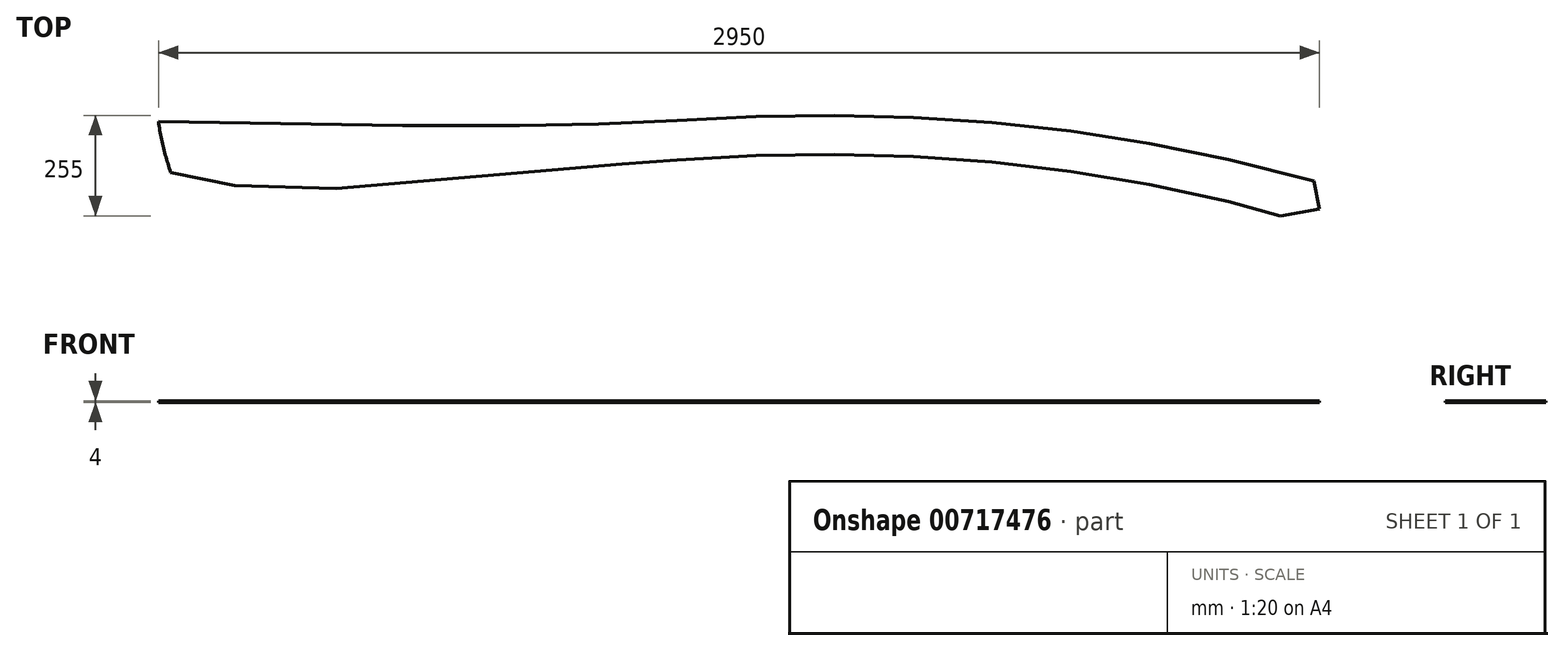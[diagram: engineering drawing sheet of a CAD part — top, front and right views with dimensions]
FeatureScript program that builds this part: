
annotation { "Feature Type Name" : "Feature", "Feature Type Description" : "" }
export const myFeature = defineFeature(function(context is Context, id is Id, definition is map)
    precondition{}
    {
        {
            var Q0;
            Q0=qCreatedBy(makeId("Top.planeOp"),FACE);
            var sketch = newSketch(context, id + "F0", { "sketchPlane" : qUnion([Q0])});
            skLineSegment(sketch, "E0", {"start": v(533, 272) * mm, "end": v(431, 192) * mm});
            skLineSegment(sketch, "E1", {"start": v(113, 312) * mm, "end": v(275, 279) * mm});
            skLineSegment(sketch, "E2", {"start": v(2933, 202) * mm, "end": v(3032, 219) * mm});
            skLineSegment(sketch, "E3", {"start": v(3017, 290) * mm, "end": v(3032, 219) * mm});
            skLineSegment(sketch, "E4", {"start": v(82, 442) * mm, "end": v(702, 431) * mm});
            skLineSegment(sketch, "E5", {"start": v(533, 272) * mm, "end": v(1260, 334) * mm});
            skLineSegment(sketch, "E6", {"start": v(275, 279) * mm, "end": v(533, 272) * mm});
            skArc(sketch, "E7", {"start": v(0, 0) * mm, "mid": v(29.12, 165.92) * mm, "end": v(113, 312) * mm});
            skArc(sketch, "E8", {"start": v(301, 0) * mm, "mid": v(294.49, 140.1) * mm, "end": v(275, 279) * mm});
            skLineSegment(sketch, "E9", {"start": v(301, 0) * mm, "end": v(0, 0) * mm});
            skArc(sketch, "E10", {"start": v(414, 0) * mm, "mid": v(418.26, 96.38) * mm, "end": v(431, 192) * mm});
            skLineSegment(sketch, "E11", {"start": v(301, 0) * mm, "end": v(414, 0) * mm});
            skPoint(sketch, "E12.orphan", {"position": v(2800, 0) * mm});
            skPoint(sketch, "E13.orphan", {"position": v(2600, 0) * mm});
            skPoint(sketch, "E14.orphan", {"position": v(2400, 0) * mm});
            skPoint(sketch, "E15.orphan", {"position": v(2200, 0) * mm});
            skPoint(sketch, "E16.orphan", {"position": v(2000, 0) * mm});
            skPoint(sketch, "E17.orphan", {"position": v(1400, 0) * mm});
            skPoint(sketch, "E18.orphan", {"position": v(1600, 0) * mm});
            skPoint(sketch, "E19.orphan", {"position": v(1800, 0) * mm});
            skLineSegment(sketch, "E20", {"start": v(1260, 334) * mm, "end": v(1400, 344) * mm});
            skLineSegment(sketch, "E21", {"start": v(1400, 344) * mm, "end": v(1600, 355) * mm});
            skLineSegment(sketch, "E22", {"start": v(1600, 355) * mm, "end": v(1800, 358) * mm});
            skLineSegment(sketch, "E23", {"start": v(1800, 358) * mm, "end": v(2000, 353) * mm});
            skLineSegment(sketch, "E24", {"start": v(2000, 353) * mm, "end": v(2200, 339) * mm});
            skLineSegment(sketch, "E25", {"start": v(2200, 339) * mm, "end": v(2400, 315) * mm});
            skLineSegment(sketch, "E26", {"start": v(2400, 315) * mm, "end": v(2600, 282) * mm});
            skLineSegment(sketch, "E27", {"start": v(2600, 282) * mm, "end": v(2800, 238) * mm});
            skLineSegment(sketch, "E28", {"start": v(2800, 238) * mm, "end": v(2933, 202) * mm});
            skLineSegment(sketch, "E29", {"start": v(3017, 290) * mm, "end": v(2800, 345) * mm});
            skLineSegment(sketch, "E30", {"start": v(2800, 345) * mm, "end": v(2600, 386) * mm});
            skLineSegment(sketch, "E31", {"start": v(2600, 386) * mm, "end": v(2400, 417) * mm});
            skLineSegment(sketch, "E32", {"start": v(2400, 417) * mm, "end": v(2200, 439) * mm});
            skLineSegment(sketch, "E33", {"start": v(2200, 439) * mm, "end": v(2000, 452) * mm});
            skLineSegment(sketch, "E34", {"start": v(2000, 452) * mm, "end": v(1800, 457) * mm});
            skLineSegment(sketch, "E35", {"start": v(1800, 457) * mm, "end": v(1600, 454) * mm});
            skLineSegment(sketch, "E36", {"start": v(1600, 454) * mm, "end": v(1400, 444) * mm});
            skLineSegment(sketch, "E37", {"start": v(702, 431) * mm, "end": v(1000, 431) * mm});
            skLineSegment(sketch, "E38", {"start": v(1000, 431) * mm, "end": v(1200, 435) * mm});
            skLineSegment(sketch, "E39", {"start": v(1200, 435) * mm, "end": v(1400, 444) * mm});
            skFitSpline(sketch, "E40", {"points": [v(82, 442) * mm, v(113, 312) * mm], "startDerivative": vector(17.06, -131.2) * mm, "endDerivative": vector(41.17, -128.02) * mm});
            skLineSegment(sketch, "E41", {"start": v(0, 0) * mm, "end": v(3878.28, 0) * mm, "construction": true});
            skSolve(sketch);
        }
        {
            var Q0;
            Q0=makeQuery(id+"F0.imprint","IMPRINT",FACE,{"disambiguationData":[TD([[makeQuery(id+"F0.imprint","IMPRINT",EDGE,{"derivedFrom":sQuery(id+"F0.wireOp",EDGE,"E1")}),1.0]])]});
            extrude(context, id + "F1", {"entities" : qUnion([Q0]), "depth" : 4 * mm, "offsetDistance" : 25 * mm});
        }
    });
